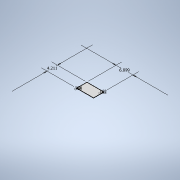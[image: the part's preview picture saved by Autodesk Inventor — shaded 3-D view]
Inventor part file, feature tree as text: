
AUTODESK INVENTOR PART (.ipt)
format: ipt  version: 2020 (Build 240168000, 168)  size: 103,936 bytes
history: native  units: in
note: dims shown in document units (in); Inventor stores cm internally (conversion verified against a paired STEP export)
features: sketch x1, extrude x1, hole x1
ambient origin geometry x8: Origin, YZ Plane, XZ Plane, XY Plane, X Axis, Y Axis, Z Axis, Center Point
bodies: Solid1 (feature_tree)
feature tree (3):
  sketch  "Sketch1"  dims[d0=6.8986in d1=4.2106in d2=0.1678in d3=0.1678in d4=0.1678in d5=0.1678in d6=0.0625in d7=0.0in d8=0.129in d9=0.224in d10=0.225in d11=0.0625in d12=0.5635in d13=0.349in d14=0.8108in]
  extrude  "Extrusion1"  Depth=4.2106in
  hole  "Hole1"  [1 undecoded]
note: 1 required parameter value undecoded (feature->parameter linkage not recoverable at this tier; creation-order binding heuristic only, values carry confidence <= 0.55)
